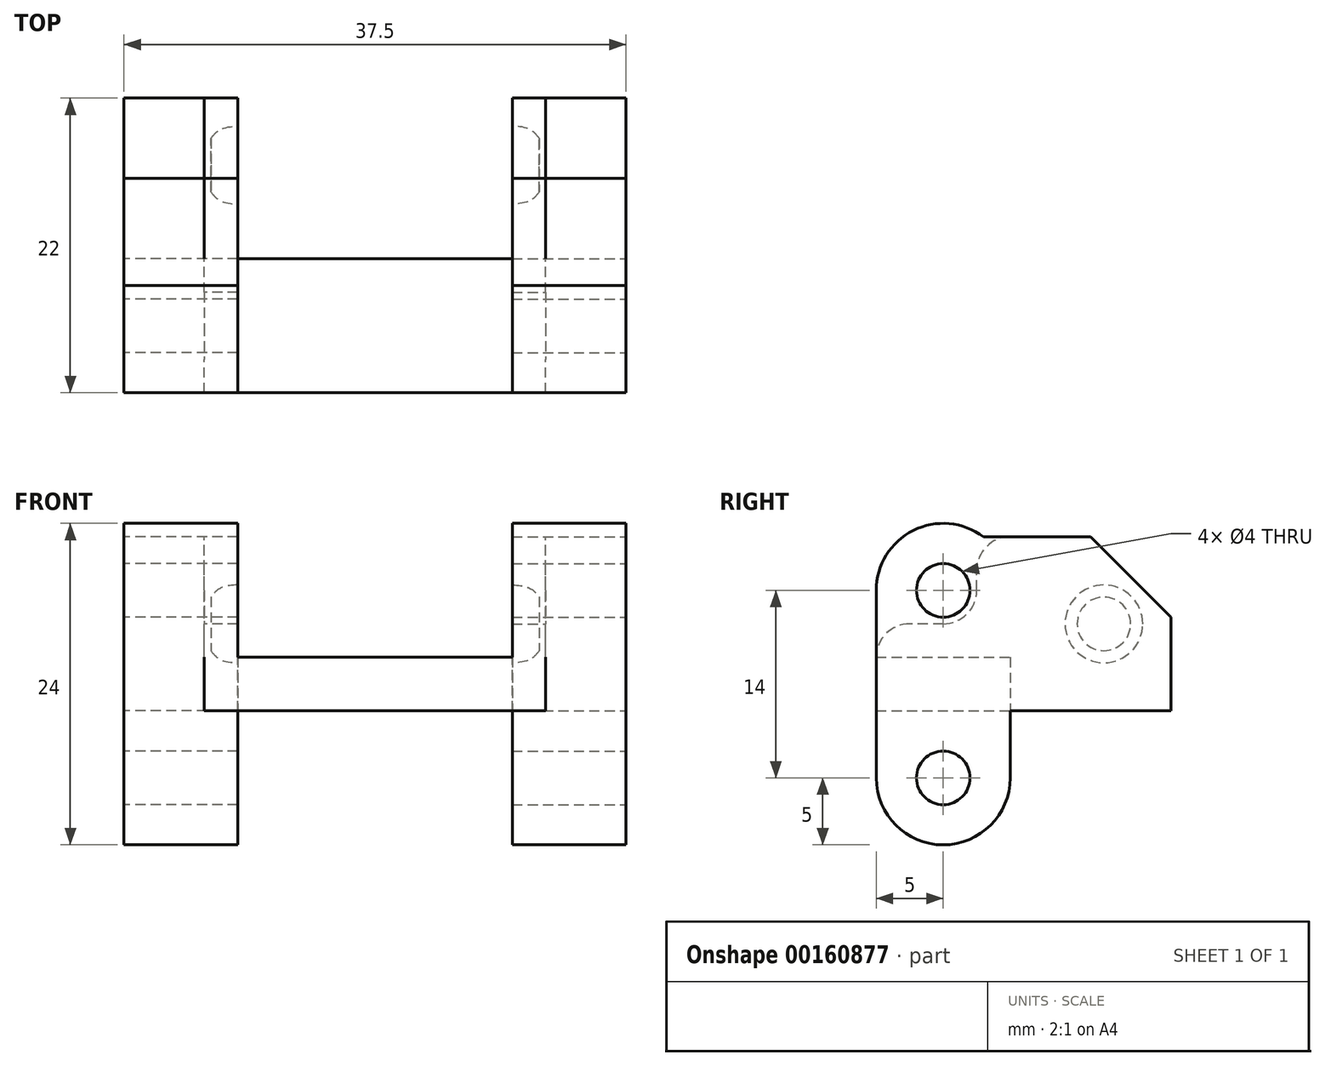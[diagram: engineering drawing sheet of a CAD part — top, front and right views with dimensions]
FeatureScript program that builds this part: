
annotation { "Feature Type Name" : "Feature", "Feature Type Description" : "" }
export const myFeature = defineFeature(function(context is Context, id is Id, definition is map)
    precondition{}
    {
        {
            var Q0;
            Q0=qCreatedBy(makeId("Top.planeOp"),FACE);
            var sketch = newSketch(context, id + "F0", { "sketchPlane" : qUnion([Q0])});
            skLineSegment(sketch, "E0.bottom", {"start": v(-12.75, 0) * mm, "end": v(12.75, 0) * mm});
            skLineSegment(sketch, "E0.top", {"start": v(-12.75, -10) * mm, "end": v(12.75, -10) * mm});
            skLineSegment(sketch, "E0.left", {"start": v(-12.75, 0) * mm, "end": v(-12.75, -10) * mm});
            skLineSegment(sketch, "E0.right", {"start": v(12.75, 0) * mm, "end": v(12.75, -10) * mm});
            skSolve(sketch);
        }
        {
            var Q0;
            Q0 = qSketchRegion(id + "F0", true);
            extrude(context, id + "F1", {"entities" : qUnion([Q0]), "depth" : 4 * mm});
        }
        {
            var Q0;
            Q0=makeQuery(id+"F1.opExtrude","SWEPT_FACE",FACE,{"disambiguationData":[OSD([sQuery(id+"F0.wireOp",EDGE,"E0.right")])]});
            var sketch = newSketch(context, id + "F2", { "sketchPlane" : qUnion([Q0])});
            skLineSegment(sketch, "E1", {"start": v(0, 0) * mm, "end": v(12, 0) * mm});
            skLineSegment(sketch, "E2", {"start": v(12, 0) * mm, "end": v(12, 7) * mm});
            skLineSegment(sketch, "E3", {"start": v(12, 7) * mm, "end": v(6, 13) * mm});
            skLineSegment(sketch, "E4", {"start": v(6, 13) * mm, "end": v(0, 13) * mm});
            skLineSegment(sketch, "E5", {"start": v(0, 13) * mm, "end": v(0, 0) * mm});
            skSolve(sketch);
        }
        {
            var Q0;
            Q0 = qSketchRegion(id + "F2", true);
            extrude(context, id + "F3", {"entities" : qUnion([Q0]), "oppositeDirection" : true, "depth" : 2.5 * mm});
        }
        {
            var Q0;
            Q0=makeQuery(id+"F3.opExtrude","CAP_FACE",FACE,{"disambiguationData":[OSD([sQuery(id+"F2.wireOp",EDGE,"E1"),sQuery(id+"F2.wireOp",EDGE,"E2"),sQuery(id+"F2.wireOp",EDGE,"E3"),sQuery(id+"F2.wireOp",EDGE,"E4"),sQuery(id+"F2.wireOp",EDGE,"E5")])],"isStart":false});
            var sketch = newSketch(context, id + "F4", { "sketchPlane" : qUnion([Q0])});
            skCircle(sketch, "E6", {"center": v(-7, 6.5) * mm, "radius": 2.9 * mm});
            skSolve(sketch);
        }
        {
            var Q0;
            Q0=makeQuery(id+"F4.imprint","IMPRINT",FACE,{"disambiguationData":[TD([[makeQuery(id+"F4.imprint","IMPRINT",EDGE,{"derivedFrom":sQuery(id+"F4.wireOp",EDGE,"E6")}),-1.0]])]});
            cPlane(context, id + "F5", {"entities" : qUnion([Q0]), "cplaneType" : CPlaneType.OFFSET, "offset" : 2 * mm, "oppositeDirection" : true, "width" : 150 * mm, "height" : 150 * mm});
        }
        {
            var Q0;
            Q0=qCreatedBy(id+"F5.planeOp",FACE);
            var sketch = newSketch(context, id + "F6", { "sketchPlane" : qUnion([Q0])});
            skCircle(sketch, "E7", {"center": v(-7, 6.5) * mm, "radius": 2 * mm});
            skSolve(sketch);
        }
        {
            var Q1;
            Q1=makeQuery(id+"F4.imprint","IMPRINT",FACE,{"disambiguationData":[TD([[makeQuery(id+"F4.imprint","IMPRINT",EDGE,{"derivedFrom":sQuery(id+"F4.wireOp",EDGE,"E6")}),1.0]])]});
            var Q2;
            Q2=makeQuery(id+"F6.imprint","IMPRINT",FACE,{"disambiguationData":[TD([[makeQuery(id+"F6.imprint","IMPRINT",EDGE,{"derivedFrom":sQuery(id+"F6.wireOp",EDGE,"E7")}),1.0]])]});
            loft(context, id + "F7", {"operationType" : NewBodyOperationType.REMOVE, "startCondition" : LoftEndDerivativeType.NORMAL_TO_PROFILE, "startMagnitude" : 2, "sheetProfilesArray" : [{ "sheetProfileEntities" : qUnion([Q1]) }, { "sheetProfileEntities" : qUnion([Q2]) }]});
        }
        {
            var Q0;
            Q0=makeQuery(id+"F3.opExtrude","SWEPT_BODY",BODY,{"disambiguationData":[OSD([sQuery(id+"F2.wireOp",EDGE,"E1"),sQuery(id+"F2.wireOp",EDGE,"E2"),sQuery(id+"F2.wireOp",EDGE,"E3"),sQuery(id+"F2.wireOp",EDGE,"E4"),sQuery(id+"F2.wireOp",EDGE,"E5")])]});
            var Q1;
            Q1=qCreatedBy(makeId("Right.planeOp"),FACE);
            mirror(context, id + "F8", {"operationType" : NewBodyOperationType.ADD, "entities" : qUnion([Q0]), "mirrorPlane" : qUnion([Q1])});
        }
        {
            var Q0;
            Q0=makeQuery(id+"F8.boolean.opBoolean","MERGE",FACE,{"derivedFrom":[makeQuery(id+"F1.opExtrude","SWEPT_FACE",FACE,{"disambiguationData":[OSD([sQuery(id+"F0.wireOp",EDGE,"E0.right")])]}),makeQuery(id+"F3.opExtrude","CAP_FACE",FACE,{"disambiguationData":[OSD([sQuery(id+"F2.wireOp",EDGE,"E1"),sQuery(id+"F2.wireOp",EDGE,"E2"),sQuery(id+"F2.wireOp",EDGE,"E3"),sQuery(id+"F2.wireOp",EDGE,"E4"),sQuery(id+"F2.wireOp",EDGE,"E5")])],"isStart":true})]});
            var sketch = newSketch(context, id + "F9", { "sketchPlane" : qUnion([Q0])});
            skLineSegment(sketch, "E8", {"start": v(-10, 4) * mm, "end": v(-10, 9) * mm});
            skLineSegment(sketch, "E9", {"start": v(0, 13) * mm, "end": v(0, 4) * mm});
            skCircle(sketch, "E10", {"center": v(-5, 9) * mm, "radius": 2 * mm});
            skPoint(sketch, "E11", {"position": v(-5, 4) * mm});
            skLineSegment(sketch, "E12", {"start": v(-10, 4) * mm, "end": v(-10, 0) * mm});
            skLineSegment(sketch, "E13", {"start": v(-10, 0) * mm, "end": v(-10, -5) * mm});
            skLineSegment(sketch, "E14", {"start": v(0, -5) * mm, "end": v(0, 0) * mm});
            skLineSegment(sketch, "E15", {"start": v(0, 0) * mm, "end": v(0, 4) * mm});
            skCircle(sketch, "E16", {"center": v(-5, -5) * mm, "radius": 2 * mm});
            skArc(sketch, "E17", {"start": v(-10, -5) * mm, "mid": v(-5, -10) * mm, "end": v(0, -5) * mm});
            skArc(sketch, "E18", {"start": v(-2, 13) * mm, "mid": v(-7.24, 13.47) * mm, "end": v(-10, 9) * mm});
            skLineSegment(sketch, "E19", {"start": v(0, 13) * mm, "end": v(-2, 13) * mm});
            skSolve(sketch);
        }
        {
            var Q0;
            Q0 = qSketchRegion(id + "F9", true);
            extrude(context, id + "F10", {"entities" : qUnion([Q0]), "operationType" : NewBodyOperationType.ADD, "oppositeDirection" : true, "depth" : 2.5 * mm});
        }
        {
            var Q0;
            Q0=makeQuery(id+"F8.boolean.opBoolean","MERGE",FACE,{"derivedFrom":[makeQuery(id+"F1.opExtrude","SWEPT_FACE",FACE,{"disambiguationData":[OSD([sQuery(id+"F0.wireOp",EDGE,"E0.left")])]}),makeQuery(id+"F8.opPattern","COPY",FACE,{"derivedFrom":makeQuery(id+"F3.opExtrude","CAP_FACE",FACE,{"disambiguationData":[OSD([sQuery(id+"F2.wireOp",EDGE,"E1"),sQuery(id+"F2.wireOp",EDGE,"E2"),sQuery(id+"F2.wireOp",EDGE,"E3"),sQuery(id+"F2.wireOp",EDGE,"E4"),sQuery(id+"F2.wireOp",EDGE,"E5")])],"isStart":true}),"instanceName":"1"})]});
            var sketch = newSketch(context, id + "F11", { "sketchPlane" : qUnion([Q0])});
            skArc(sketch, "E20", {"start": v(2.5, 9) * mm, "mid": v(3.23, 7.23) * mm, "end": v(5, 6.5) * mm});
            skArc(sketch, "E21", {"start": v(2.5, 10.5) * mm, "mid": v(1.77, 12.27) * mm, "end": v(0, 13) * mm});
            skLineSegment(sketch, "E22", {"start": v(2.5, 9) * mm, "end": v(2.5, 10.5) * mm});
            skLineSegment(sketch, "E23", {"start": v(0, 13) * mm, "end": v(0, 4) * mm});
            skLineSegment(sketch, "E24", {"start": v(0, 4) * mm, "end": v(10, 4) * mm});
            skArc(sketch, "E25", {"start": v(10, 4) * mm, "mid": v(9.27, 5.77) * mm, "end": v(7.5, 6.5) * mm});
            skLineSegment(sketch, "E26", {"start": v(5, 6.5) * mm, "end": v(7.5, 6.5) * mm});
            skSolve(sketch);
        }
        {
            var Q0;
            Q0 = qSketchRegion(id + "F11", true);
            extrude(context, id + "F12", {"entities" : qUnion([Q0]), "operationType" : NewBodyOperationType.ADD, "oppositeDirection" : true, "depth" : 2.5 * mm});
        }
        {
            var Q0;
            Q0=makeQuery(id+"F10.boolean.opBoolean","MERGE",FACE,{"derivedFrom":[makeQuery(id+"F8.boolean.opBoolean","MERGE",FACE,{"derivedFrom":[makeQuery(id+"F1.opExtrude","SWEPT_FACE",FACE,{"disambiguationData":[OSD([sQuery(id+"F0.wireOp",EDGE,"E0.right")])]}),makeQuery(id+"F3.opExtrude","CAP_FACE",FACE,{"disambiguationData":[OSD([sQuery(id+"F2.wireOp",EDGE,"E1"),sQuery(id+"F2.wireOp",EDGE,"E2"),sQuery(id+"F2.wireOp",EDGE,"E3"),sQuery(id+"F2.wireOp",EDGE,"E4"),sQuery(id+"F2.wireOp",EDGE,"E5")])],"isStart":true})]}),makeQuery(id+"F10.opExtrude","CAP_FACE",FACE,{"disambiguationData":[OSD([sQuery(id+"F9.wireOp",EDGE,"E8"),sQuery(id+"F9.wireOp",EDGE,"E9"),sQuery(id+"F9.wireOp",EDGE,"E10"),sQuery(id+"F9.wireOp",EDGE,"E12"),sQuery(id+"F9.wireOp",EDGE,"E13"),sQuery(id+"F9.wireOp",EDGE,"E14"),sQuery(id+"F9.wireOp",EDGE,"E15"),sQuery(id+"F9.wireOp",EDGE,"E16"),sQuery(id+"F9.wireOp",EDGE,"E17"),sQuery(id+"F9.wireOp",EDGE,"E18"),sQuery(id+"F9.wireOp",EDGE,"E19")])],"isStart":true})]});
            var sketch = newSketch(context, id + "F13", { "sketchPlane" : qUnion([Q0])});
            skLineSegment(sketch, "E27", {"start": v(-2, 13) * mm, "end": v(6, 13) * mm});
            skLineSegment(sketch, "E28", {"start": v(6, 13) * mm, "end": v(12, 7) * mm});
            skLineSegment(sketch, "E29", {"start": v(12, 7) * mm, "end": v(12, 0) * mm});
            skLineSegment(sketch, "E30", {"start": v(12, 0) * mm, "end": v(0, 0) * mm});
            skLineSegment(sketch, "E31", {"start": v(0, 0) * mm, "end": v(0, -5) * mm});
            skLineSegment(sketch, "E32", {"start": v(-10, 9) * mm, "end": v(-10, -5) * mm});
            skArc(sketch, "E33", {"start": v(-2, 13) * mm, "mid": v(-7.24, 13.47) * mm, "end": v(-10, 9) * mm});
            skArc(sketch, "E34", {"start": v(-10, -5) * mm, "mid": v(-5, -10) * mm, "end": v(0, -5) * mm});
            skCircle(sketch, "E35", {"center": v(-5, 9) * mm, "radius": 2 * mm});
            skCircle(sketch, "E36", {"center": v(-5, -5) * mm, "radius": 2 * mm});
            skSolve(sketch);
        }
        {
            var Q0;
            Q0 = qSketchRegion(id + "F13", true);
            extrude(context, id + "F14", {"entities" : qUnion([Q0]), "operationType" : NewBodyOperationType.ADD, "depth" : 6 * mm});
        }
        {
            var Q0;
            Q0=makeQuery(id+"F1.opExtrude","SWEPT_BODY",BODY,{"disambiguationData":[OSD([sQuery(id+"F0.wireOp",EDGE,"E0.bottom"),sQuery(id+"F0.wireOp",EDGE,"E0.top"),sQuery(id+"F0.wireOp",EDGE,"E0.left"),sQuery(id+"F0.wireOp",EDGE,"E0.right")])]});
            var Q1;
            Q1=qCreatedBy(makeId("Right.planeOp"),FACE);
            mirror(context, id + "F15", {"entities" : qUnion([Q0]), "mirrorPlane" : qUnion([Q1])});
        }
    });
